# Revit family: Electronics_Amplifiers_Biamp_Vocia_VA-4030e___
name_source: partatom
category: Communication Devices
units: mm (PartAtom-declared; Revit-internal decimal feet)

## family parameters
Cut with Voids When Loaded = Yes
Host = Face
Maintain Annotation Orientation = No
OmniClass Number = 23.85.10.11.14.14.17
OmniClass Title = Sound Amplifiers
Part Type = Normal
Room Calculation Point = No
Round Connector Dimension = Use Diameter
Shared = No

## types (1)
- VA-4030e
    Altitude = 0-10,000 ft (0-3000m) MSL
    Apparent Load = 60 VA
    Back Panel = Yes
    Compliance = EN 54-16 certified FCC Part 15B (USA) CE marked (Europe) RCM (Australia) EAC (Eurasian Customs Union) RoHS. Directive (Europe) RINA (Italy) EN 60849, AS 60849 verified
    Connector Description = 100-240VAC; 50/60Hz
    Default Elevation = 48 "
    Depth = 14.2 "
    Description = Vocia® VA-4030e Amplifier
    Frequency Response = ± 2dB
    Height = 3.25 "
    Housing Material = Biamp - Metal - Silver
    Humidity = 0-95% relative humidity (non-condensing)
    Inputs = 20 bits, 48 kHz, 5-1/3 ms (fixed)
    Manufacturer = Biamp
    Max Power Consumption = 60 W
    Memory = 5.625 MB
    Model = Vocia VA-4030e
    Network Connection = RJ-45 with shielded Ethernet (CAT5, CAT5e, CAT6 or CAT7
    Number of Poles = 1
    Power Factor = 1
    Product Documentation Link = https://downloads.biamp.com
    Product Page URL = https://www.biamp.com
    Product data url = https://www.bimobject.com
    Signal to Noise Ratio = > 88 dB, unweighted
    THD+N = 50Hz-100Hz: < 0.5%; 100Hz-10kHz: < 0.3%
    Temperature Range = 23 - 104° F (-5 - 40° C)
    Total Output Power = 4 x 30W RMS, 120W maximum
    URL = https://www.biamp.com
    Voltage = 120 V
    Weight = 26.20 lbf
    Width = 19 "

## geometry (parser evidence)
native form markers: Sweep x4
no freeform markers — native parametric forms only
